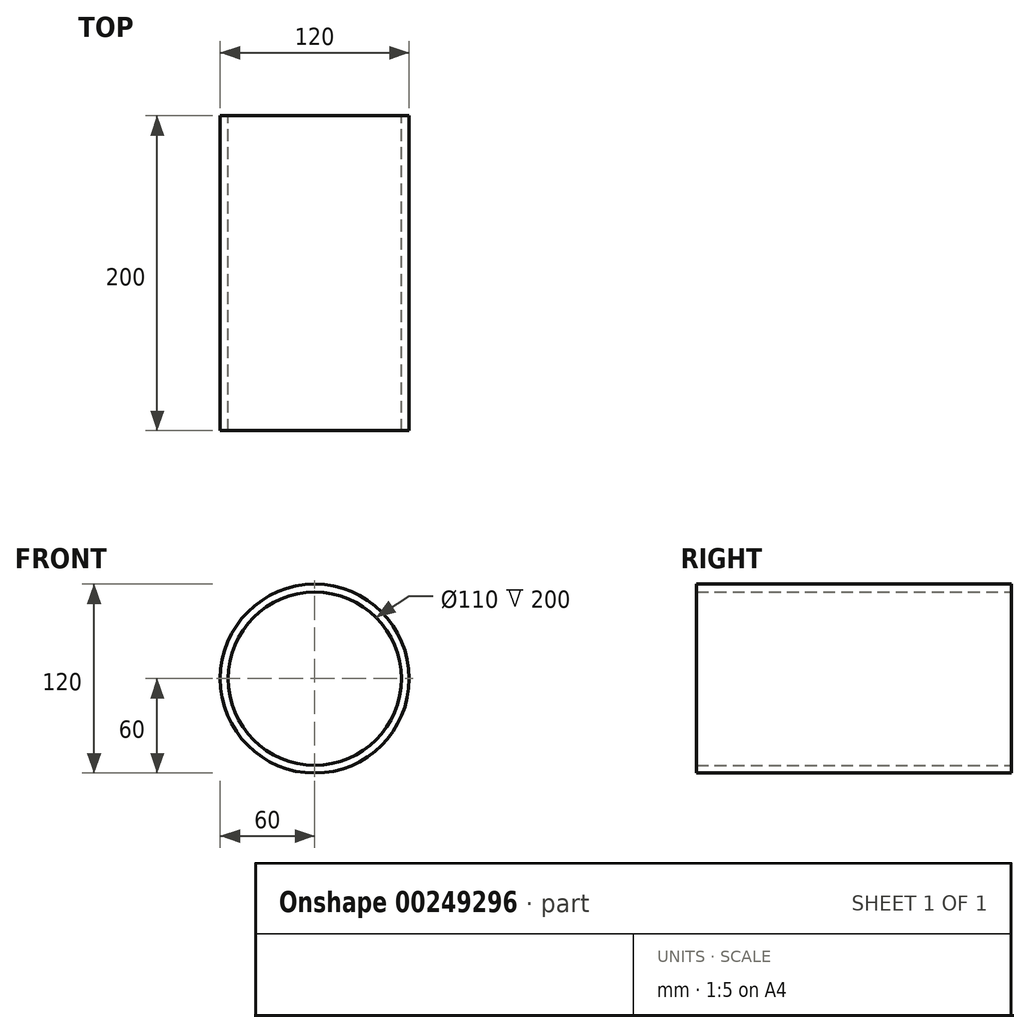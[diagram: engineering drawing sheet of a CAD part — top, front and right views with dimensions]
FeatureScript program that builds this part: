
annotation { "Feature Type Name" : "Feature", "Feature Type Description" : "" }
export const myFeature = defineFeature(function(context is Context, id is Id, definition is map)
    precondition{}
    {
        {
            var Q0;
            Q0=qCreatedBy(makeId("Front.planeOp"),FACE);
            var sketch = newSketch(context, id + "F0", { "sketchPlane" : qUnion([Q0])});
            skCircle(sketch, "E0", {"center": v(0, 0) * mm, "radius": 55 * mm});
            skCircle(sketch, "E1", {"center": v(0, 0) * mm, "radius": 60 * mm});
            skSolve(sketch);
        }
        {
            var Q0;
            Q0=makeQuery(id+"F0.imprint","IMPRINT",FACE,{"disambiguationData":[TD([[makeQuery(id+"F0.imprint","IMPRINT",EDGE,{"derivedFrom":sQuery(id+"F0.wireOp",EDGE,"E0")}),-1.0]])]});
            extrude(context, id + "F1", {"entities" : qUnion([Q0]), "depth" : 200 * mm, "offsetDistance" : 25 * mm, "symmetric" : true});
        }
    });
